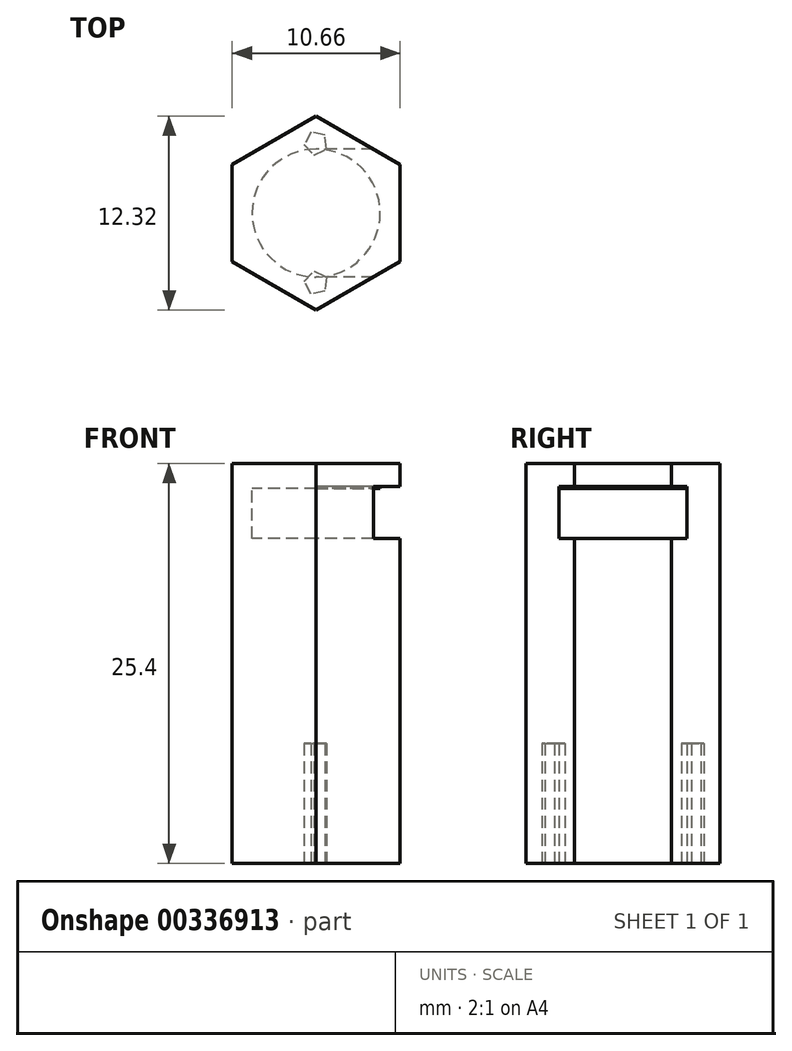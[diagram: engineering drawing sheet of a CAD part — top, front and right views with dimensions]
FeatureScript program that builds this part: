
annotation { "Feature Type Name" : "Feature", "Feature Type Description" : "" }
export const myFeature = defineFeature(function(context is Context, id is Id, definition is map)
    precondition{}
    {
        {
            var Q0;
            Q0=qCreatedBy(makeId("Top.planeOp"),FACE);
            var sketch = newSketch(context, id + "F0", { "sketchPlane" : qUnion([Q0])});
            skCircle(sketch, "E0.cCircle", {"center": v(0, 0) * mm, "radius": 5.33 * mm, "construction": true});
            skLineSegment(sketch, "E0.0", {"start": v(5.33, 3.08) * mm, "end": v(5.33, -3.08) * mm});
            skLineSegment(sketch, "E0.1", {"start": v(5.33, -3.08) * mm, "end": v(0, -6.16) * mm});
            skLineSegment(sketch, "E0.2", {"start": v(0, -6.16) * mm, "end": v(-5.33, -3.08) * mm});
            skLineSegment(sketch, "E0.3", {"start": v(-5.33, -3.08) * mm, "end": v(-5.33, 3.08) * mm});
            skLineSegment(sketch, "E0.4", {"start": v(-5.33, 3.08) * mm, "end": v(0, 6.16) * mm});
            skLineSegment(sketch, "E0.5", {"start": v(0, 6.16) * mm, "end": v(5.33, 3.08) * mm});
            skPoint(sketch, "E0.0.midPoint", {"position": v(5.33, 0) * mm});
            skSolve(sketch);
        }
        {
            var Q0;
            Q0 = qSketchRegion(id + "F0", true);
            extrude(context, id + "F1", {"entities" : qUnion([Q0]), "depth" : 25.4 * mm});
        }
        {
            var Q0;
            Q0=makeQuery(id+"F1.opExtrude","CAP_FACE",FACE,{"disambiguationData":[OSD([sQuery(id+"F0.wireOp",EDGE,"E0.0"),sQuery(id+"F0.wireOp",EDGE,"E0.1"),sQuery(id+"F0.wireOp",EDGE,"E0.2"),sQuery(id+"F0.wireOp",EDGE,"E0.3"),sQuery(id+"F0.wireOp",EDGE,"E0.4"),sQuery(id+"F0.wireOp",EDGE,"E0.5")])],"isStart":false});
            var sketch = newSketch(context, id + "F2", { "sketchPlane" : qUnion([Q0])});
            skCircle(sketch, "E1", {"center": v(0, 0) * mm, "radius": 4.06 * mm});
            skSolve(sketch);
        }
        {
            var Q0;
            Q0 = qSketchRegion(id + "F2", true);
            extrude(context, id + "F3", {"entities" : qUnion([Q0]), "operationType" : NewBodyOperationType.REMOVE, "oppositeDirection" : true, "depth" : 4.76 * mm});
        }
        {
            var Q0;
            Q0=qCreatedBy(makeId("Right.planeOp"),FACE);
            var sketch = newSketch(context, id + "F4", { "sketchPlane" : qUnion([Q0])});
            skLineSegment(sketch, "E2.bottom", {"start": v(-4.06, 23.94) * mm, "end": v(4.06, 23.94) * mm});
            skLineSegment(sketch, "E2.top", {"start": v(-4.06, 20.64) * mm, "end": v(4.06, 20.64) * mm});
            skLineSegment(sketch, "E2.left", {"start": v(-4.06, 23.94) * mm, "end": v(-4.06, 20.64) * mm});
            skLineSegment(sketch, "E2.right", {"start": v(4.06, 23.94) * mm, "end": v(4.06, 20.64) * mm});
            skLineSegment(sketch, "E3", {"start": v(0, 23.94) * mm, "end": v(0, 20.64) * mm, "construction": true});
            skSolve(sketch);
        }
        {
            var Q0;
            Q0 = qSketchRegion(id + "F4", true);
            extrude(context, id + "F5", {"entities" : qUnion([Q0]), "operationType" : NewBodyOperationType.REMOVE, "endBound" : BoundingType.THROUGH_ALL, "depth" : 25.4 * mm});
        }
        {
            var Q0;
            Q0=makeQuery(id+"F1.opExtrude","CAP_FACE",FACE,{"disambiguationData":[OSD([sQuery(id+"F0.wireOp",EDGE,"E0.0"),sQuery(id+"F0.wireOp",EDGE,"E0.1"),sQuery(id+"F0.wireOp",EDGE,"E0.2"),sQuery(id+"F0.wireOp",EDGE,"E0.3"),sQuery(id+"F0.wireOp",EDGE,"E0.4"),sQuery(id+"F0.wireOp",EDGE,"E0.5")])],"isStart":false});
            var sketch = newSketch(context, id + "F6", { "sketchPlane" : qUnion([Q0])});
            skCircle(sketch, "E4", {"center": v(0, 0) * mm, "radius": 4.06 * mm});
            skSolve(sketch);
        }
        {
            var Q0;
            Q0 = qSketchRegion(id + "F6", true);
            extrude(context, id + "F7", {"entities" : qUnion([Q0]), "operationType" : NewBodyOperationType.ADD, "oppositeDirection" : true, "depth" : 1.59 * mm});
        }
        {
            var Q0;
            Q0=makeQuery(id+"F1.opExtrude","CAP_FACE",FACE,{"disambiguationData":[OSD([sQuery(id+"F0.wireOp",EDGE,"E0.0"),sQuery(id+"F0.wireOp",EDGE,"E0.1"),sQuery(id+"F0.wireOp",EDGE,"E0.2"),sQuery(id+"F0.wireOp",EDGE,"E0.3"),sQuery(id+"F0.wireOp",EDGE,"E0.4"),sQuery(id+"F0.wireOp",EDGE,"E0.5")])],"isStart":true});
            var sketch = newSketch(context, id + "F8", { "sketchPlane" : qUnion([Q0])});
            skLineSegment(sketch, "E5", {"start": v(0, 0) * mm, "end": v(5.33, 0) * mm, "construction": true});
            skCircle(sketch, "E6.cCircle", {"center": v(0, -4.45) * mm, "radius": 0.76 * mm, "construction": true});
            skLineSegment(sketch, "E6.0", {"start": v(0.66, -4.07) * mm, "end": v(0.56, -4.96) * mm});
            skLineSegment(sketch, "E6.1", {"start": v(0.56, -4.96) * mm, "end": v(-0.32, -5.14) * mm});
            skLineSegment(sketch, "E6.2", {"start": v(-0.32, -5.14) * mm, "end": v(-0.76, -4.36) * mm});
            skLineSegment(sketch, "E6.3", {"start": v(-0.76, -4.36) * mm, "end": v(-0.15, -3.7) * mm});
            skLineSegment(sketch, "E6.4", {"start": v(-0.15, -3.7) * mm, "end": v(0.66, -4.07) * mm});
            skLineSegment(sketch, "E7.MirrorCS", {"start": v(0.66, 4.07) * mm, "end": v(0.56, 4.96) * mm});
            skLineSegment(sketch, "E8.MirrorCS", {"start": v(-0.15, 3.7) * mm, "end": v(0.66, 4.07) * mm});
            skLineSegment(sketch, "E9.MirrorCS", {"start": v(0.56, 4.96) * mm, "end": v(-0.32, 5.14) * mm});
            skLineSegment(sketch, "E10.MirrorCS", {"start": v(-0.76, 4.36) * mm, "end": v(-0.15, 3.7) * mm});
            skCircle(sketch, "E11.MirrorC", {"center": v(0, 4.45) * mm, "radius": 0.76 * mm, "construction": true});
            skLineSegment(sketch, "E12.MirrorCS", {"start": v(-0.32, 5.14) * mm, "end": v(-0.76, 4.36) * mm});
            skSolve(sketch);
        }
        {
            var Q0;
            Q0 = qSketchRegion(id + "F8", true);
            extrude(context, id + "F9", {"entities" : qUnion([Q0]), "operationType" : NewBodyOperationType.REMOVE, "oppositeDirection" : true, "depth" : 7.62 * mm});
        }
    });
